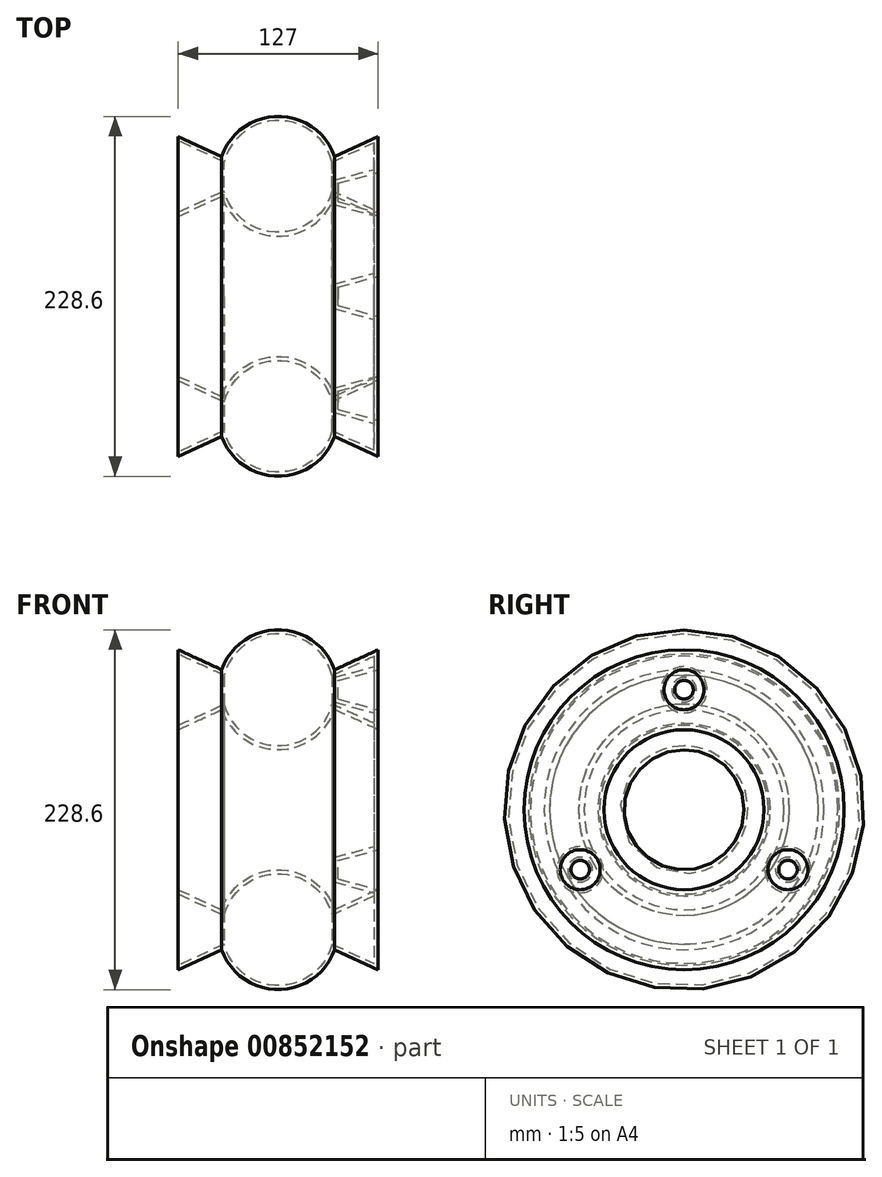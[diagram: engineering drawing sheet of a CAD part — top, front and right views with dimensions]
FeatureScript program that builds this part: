
annotation { "Feature Type Name" : "Feature", "Feature Type Description" : "" }
export const myFeature = defineFeature(function(context is Context, id is Id, definition is map)
    precondition{}
    {
        {
            var Q0;
            Q0=qCreatedBy(makeId("Front.planeOp"),FACE);
            var sketch = newSketch(context, id + "F0", { "sketchPlane" : qUnion([Q0])});
            skArc(sketch, "E0", {"start": v(-35.92, -12.7) * mm, "mid": v(0, -38.1) * mm, "end": v(35.92, -12.7) * mm});
            skLineSegment(sketch, "E1", {"start": v(35.92, 12.7) * mm, "end": v(63.5, 25.4) * mm});
            skLineSegment(sketch, "E2", {"start": v(63.5, 25.4) * mm, "end": v(63.5, -25.4) * mm});
            skLineSegment(sketch, "E3", {"start": v(63.5, -25.4) * mm, "end": v(35.92, -12.7) * mm});
            skLineSegment(sketch, "E4.MirrorCS", {"start": v(-63.5, 25.4) * mm, "end": v(-63.5, -25.4) * mm});
            skLineSegment(sketch, "E5.MirrorCS", {"start": v(-63.5, -25.4) * mm, "end": v(-35.92, -12.7) * mm});
            skLineSegment(sketch, "E6.MirrorCS", {"start": v(-35.92, 12.7) * mm, "end": v(-63.5, 25.4) * mm});
            skArc(sketch, "E7.trimOffspring", {"start": v(35.92, 12.7) * mm, "mid": v(0, 38.1) * mm, "end": v(-35.92, 12.7) * mm});
            skLineSegment(sketch, "E8", {"start": v(-63.5, 76.2) * mm, "end": v(63.5, 76.2) * mm, "construction": true});
            skSolve(sketch);
        }
        {
            var Q0;
            Q0=makeQuery(id+"F0.imprint","IMPRINT",FACE,{"disambiguationData":[TD([[makeQuery(id+"F0.imprint","IMPRINT",EDGE,{"derivedFrom":sQuery(id+"F0.wireOp",EDGE,"E0")}),1.0]])]});
            var Q1;
            Q1=sQuery(id+"F0.wireOp",EDGE,"E8");
            revolve(context, id + "F1", {"surfaceOperationType" : NewSurfaceOperationType.NEW, "entities" : qUnion([Q0]), "axis" : qUnion([Q1]), "revolveType" : RevolveType.FULL});
        }
        {
            var Q0;
            Q0=makeQuery(id+"F1.opRevolve","SWEPT_FACE",FACE,{"disambiguationData":[OSD([sQuery(id+"F0.wireOp",EDGE,"E2")])]});
            var sketch = newSketch(context, id + "F2", { "sketchPlane" : qUnion([Q0])});
            skCircle(sketch, "E9", {"center": v(0, 152.4) * mm, "radius": 12.7 * mm});
            skLineSegment(sketch, "E10", {"start": v(0, 177.8) * mm, "end": v(0, 127) * mm, "construction": true});
            skCircle(sketch, "E11.1.0", {"center": v(-66, 38.1) * mm, "radius": 12.7 * mm});
            skCircle(sketch, "E11.2.0", {"center": v(66, 38.1) * mm, "radius": 12.7 * mm});
            skPoint(sketch, "E11.center", {"position": v(0, 76.2) * mm});
            skSolve(sketch);
        }
        {
            var Q0;
            Q0 = qSketchRegion(id + "F2", true);
            extrude(context, id + "F3", {"entities" : qUnion([Q0]), "operationType" : NewBodyOperationType.REMOVE, "oppositeDirection" : true, "depth" : 25.4 * mm, "offsetDistance" : 25.4 * mm, "hasDraft" : true, "draftAngle" : 15 * degree, "draftPullDirection" : true});
        }
        {
            var Q0;
            Q0=makeQuery(id+"F1.opRevolve","SWEPT_FACE",FACE,{"disambiguationData":[OSD([sQuery(id+"F0.wireOp",EDGE,"E4.MirrorCS")])]});
            shell(context, id + "F4", {"entities" : qUnion([Q0]), "thickness" : 2.54 * mm});
        }
    });
